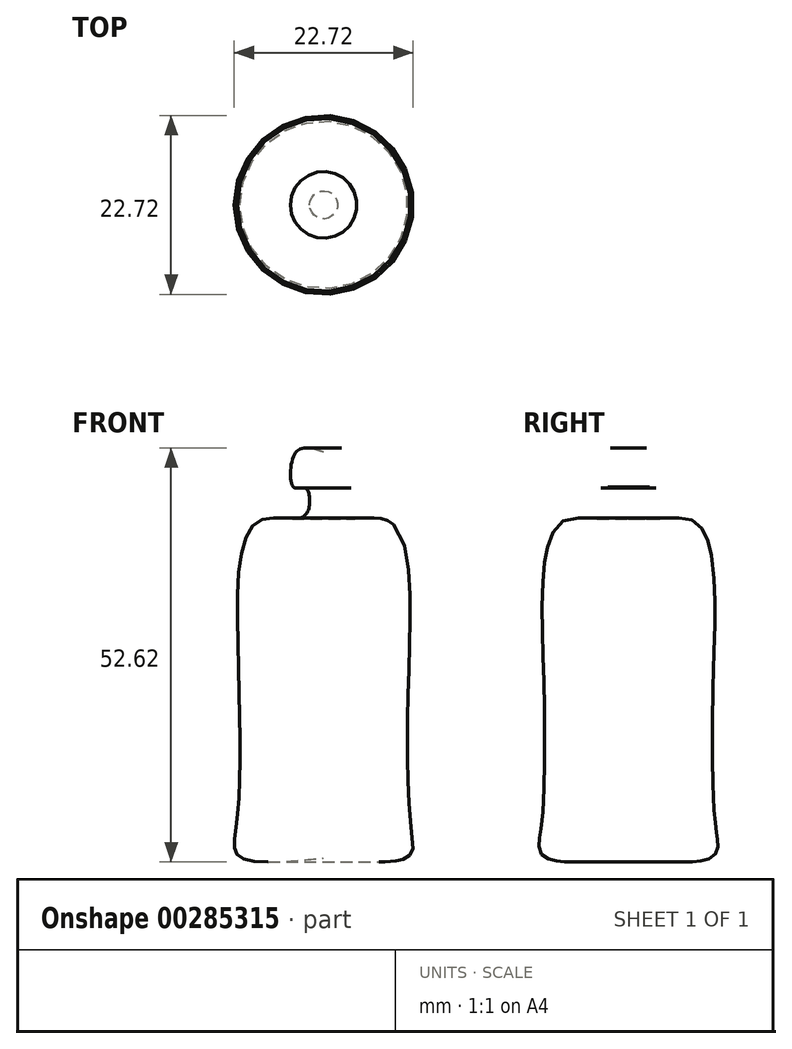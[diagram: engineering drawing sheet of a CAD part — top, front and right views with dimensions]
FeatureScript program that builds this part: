
annotation { "Feature Type Name" : "Feature", "Feature Type Description" : "" }
export const myFeature = defineFeature(function(context is Context, id is Id, definition is map)
    precondition{}
    {
        {
            var Q0;
            Q0=qCreatedBy(makeId("Front.planeOp"),FACE);
            var sketch = newSketch(context, id + "F0", { "sketchPlane" : qUnion([Q0])});
            skLineSegment(sketch, "E0", {"start": v(0, 76.05) * mm, "end": v(0, 0) * mm, "construction": true});
            skFitSpline(sketch, "E1", {"points": [v(0, 62.4) * mm, v(-3.53, 62.4) * mm, v(-3.77, 57.93) * mm, v(-2.35, 57.93) * mm, v(-2.35, 54.4) * mm, v(-8.24, 53.7) * mm, v(-10.83, 35.33) * mm, v(-11.06, 15.09) * mm, v(-10.83, 11.09) * mm, v(0, 10.85) * mm], "startDerivative": vector(-52.23, 18.16) * mm, "endDerivative": vector(101.37, 10.18) * mm});
            skLineSegment(sketch, "E2", {"start": v(0, 62.4) * mm, "end": v(0, 10.85) * mm});
            skSolve(sketch);
        }
        {
            var Q0;
            Q0 = qSketchRegion(id + "F0", true);
            var Q1;
            Q1=sQuery(id+"F0.wireOp",EDGE,"E2");
            revolve(context, id + "F1", {"entities" : qUnion([Q0]), "axis" : qUnion([Q1]), "revolveType" : RevolveType.FULL});
        }
    });
